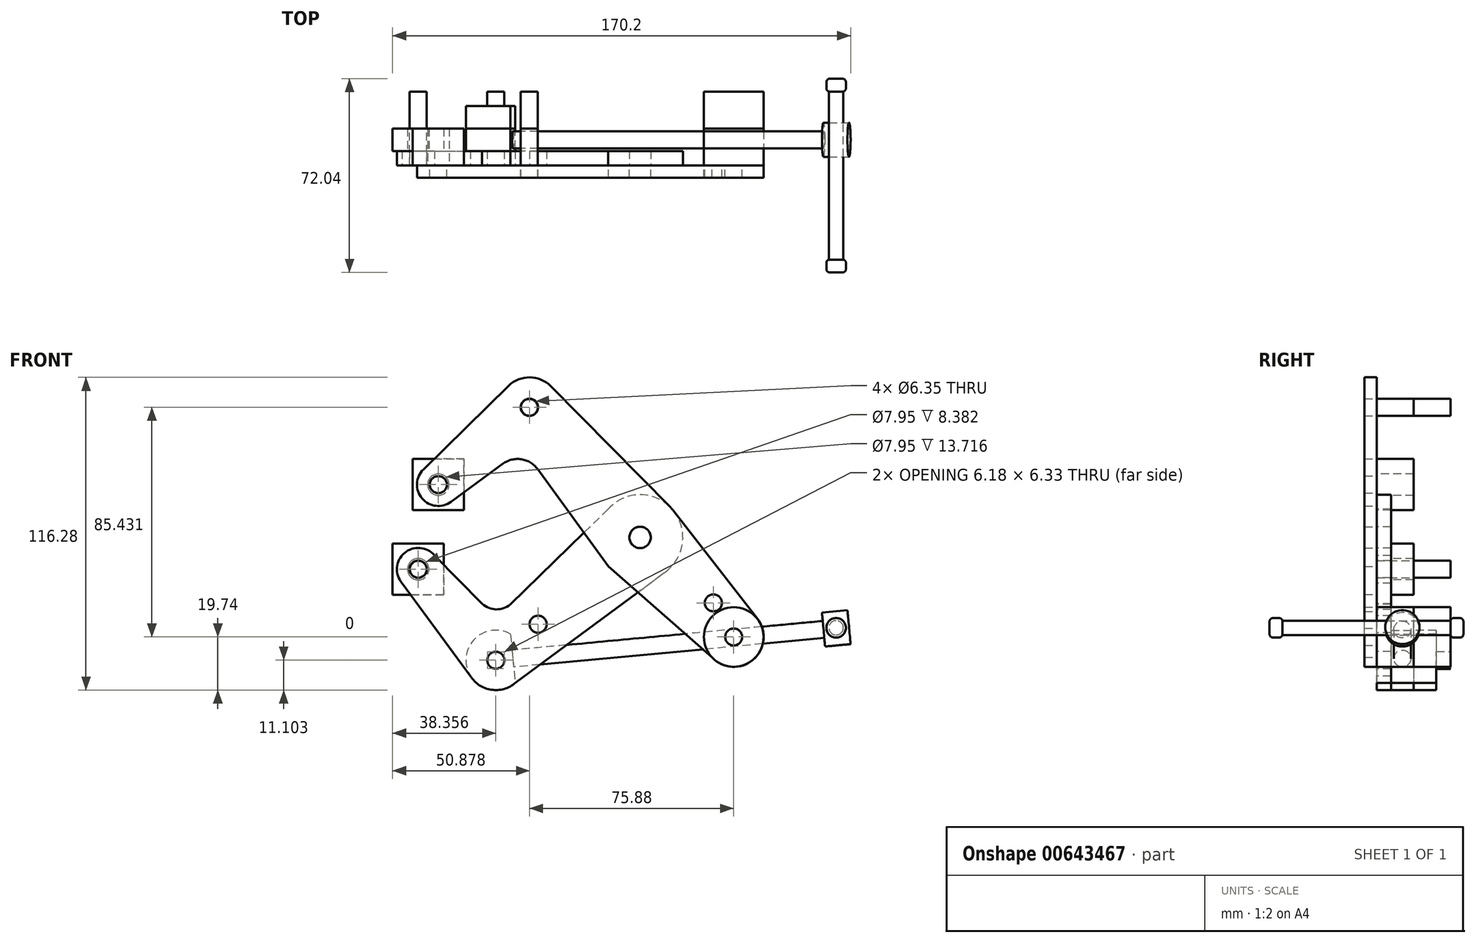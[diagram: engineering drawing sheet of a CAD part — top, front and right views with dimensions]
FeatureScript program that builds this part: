
annotation { "Feature Type Name" : "Feature", "Feature Type Description" : "" }
export const myFeature = defineFeature(function(context is Context, id is Id, definition is map)
    precondition{}
    {
        {
            var Q0;
            Q0=qCreatedBy(makeId("Front.planeOp"),FACE);
            var sketch = newSketch(context, id + "F0", { "sketchPlane" : qUnion([Q0])});
            skCircle(sketch, "E0", {"center": v(0, 0) * mm, "radius": 3.98 * mm});
            skCircle(sketch, "E1", {"center": v(0, 0) * mm, "radius": 15.88 * mm});
            skCircle(sketch, "E2", {"center": v(-41.1, 48.41) * mm, "radius": 11.11 * mm});
            skCircle(sketch, "E3", {"center": v(-41.1, 48.41) * mm, "radius": 3.18 * mm});
            skCircle(sketch, "E4", {"center": v(-74.97, 19.63) * mm, "radius": 3.18 * mm});
            skCircle(sketch, "E5", {"center": v(-74.97, 19.63) * mm, "radius": 7.94 * mm});
            skCircle(sketch, "E6", {"center": v(0, 0) * mm, "radius": 3.18 * mm});
            skCircle(sketch, "E7", {"center": v(34.79, -37.02) * mm, "radius": 3.18 * mm});
            skCircle(sketch, "E8", {"center": v(34.79, -37.02) * mm, "radius": 11.11 * mm});
            skLineSegment(sketch, "E9", {"start": v(-41.1, 48.41) * mm, "end": v(-74.97, 19.63) * mm, "construction": true});
            skLineSegment(sketch, "E10", {"start": v(-41.1, 48.41) * mm, "end": v(0, 0) * mm, "construction": true});
            skLineSegment(sketch, "E11", {"start": v(0, 0) * mm, "end": v(34.79, -37.02) * mm, "construction": true});
            skCircle(sketch, "E12", {"center": v(27.23, -24.34) * mm, "radius": 3.18 * mm});
            skLineSegment(sketch, "E13", {"start": v(-33.18, 56.22) * mm, "end": v(11.3, 11.15) * mm});
            skLineSegment(sketch, "E14", {"start": v(12.54, 9.74) * mm, "end": v(43.56, -30.2) * mm});
            skLineSegment(sketch, "E15", {"start": v(26.69, -44.63) * mm, "end": v(-11.8, -10.76) * mm});
            skLineSegment(sketch, "E16", {"start": v(-11.8, -10.76) * mm, "end": v(-38.09, 25.38) * mm});
            skLineSegment(sketch, "E17", {"start": v(-80.52, 25.3) * mm, "end": v(-48.87, 56.34) * mm});
            skPoint(sketch, "E18", {"position": v(-43.61, 32.78) * mm});
            skPoint(sketch, "E19", {"position": v(-80.25, 58.74) * mm});
            skArc(sketch, "E20", {"start": v(-38.09, 25.38) * mm, "mid": v(-44.1, 29.06) * mm, "end": v(-50.97, 27.39) * mm});
            skLineSegment(sketch, "E21", {"start": v(-50.97, 27.39) * mm, "end": v(-70.27, 13.23) * mm});
            skSolve(sketch);
        }
        {
            var Q0;
            Q0 = qSketchRegion(id + "F0", true);
            var Q1;
            {var subQ1=sQuery(id+"F0.wireOp",EDGE,"pfiCSikp-8CTO-SDfE-DP6H-Jw97YbxvFowv");var subQ3=sQuery(id+"F0.wireOp",EDGE,"inh5m93a-XSK5-ioNv-JxQd-0MRj083akBz5");var subQ4=makeQuery(id+"F0.imprint","INTERSECT",VERTEX,{"derivedFrom":[subQ1,subQ3]});Q1=makeQuery(id+"F0.imprint","IMPRINT",FACE,{"disambiguationData":[TD([[makeQuery(id+"F0.imprint","IMPRINT",EDGE,{"disambiguationData":[TD([[subQ4,1.0]])],"derivedFrom":subQ3}),-1.0]])]});}
            var Q2;
            {var subQ5=sQuery(id+"F0.wireOp",EDGE,"1JsmmwyK-uvK5-ssic-tOmo-jzBYzs2uoYHw");var subQ7=sQuery(id+"F0.wireOp",EDGE,"MQRNNOWK-pdrb-iC6u-Mh0e-8VP2wnjC3u4w");var subQ8=makeQuery(id+"F0.imprint","INTERSECT",VERTEX,{"derivedFrom":[subQ5,subQ7]});Q2=makeQuery(id+"F0.imprint","IMPRINT",FACE,{"disambiguationData":[TD([[makeQuery(id+"F0.imprint","IMPRINT",EDGE,{"disambiguationData":[TD([[subQ8,1.0]])],"derivedFrom":subQ5}),-1.0]])]});}
            extrude(context, id + "F1", {"entities" : qUnion([Q0, Q1, Q2]), "depth" : 4.57 * mm, "offsetDistance" : 25.4 * mm});
        }
        {
            var Q0;
            Q0=qCreatedBy(makeId("Front.planeOp"),FACE);
            var sketch = newSketch(context, id + "F2", { "sketchPlane" : qUnion([Q0])});
            skCircle(sketch, "E22", {"center": v(0, -0.01) * mm, "radius": 15.88 * mm});
            skCircle(sketch, "E23", {"center": v(-53.62, -45.66) * mm, "radius": 3.18 * mm});
            skCircle(sketch, "E24", {"center": v(-37.9, -32.27) * mm, "radius": 3.18 * mm});
            skCircle(sketch, "E25", {"center": v(-82.44, -11.83) * mm, "radius": 3.18 * mm});
            skCircle(sketch, "E26", {"center": v(-82.44, -11.83) * mm, "radius": 7.94 * mm});
            skLineSegment(sketch, "E27", {"start": v(-76.4, -6.68) * mm, "end": v(-76.4, -6.68) * mm});
            skLineSegment(sketch, "E28", {"start": v(-88.49, -16.97) * mm, "end": v(-62.08, -52.87) * mm});
            skLineSegment(sketch, "E29", {"start": v(-46.41, -54.12) * mm, "end": v(10.96, -11.66) * mm});
            skArc(sketch, "E30", {"start": v(-58.68, -24.7) * mm, "mid": v(-53.52, -26.75) * mm, "end": v(-48.26, -24.95) * mm});
            skPoint(sketch, "E31", {"position": v(-53.46, -30.01) * mm});
            skPoint(sketch, "E32", {"position": v(-10.2, 12.15) * mm});
            skLineSegment(sketch, "E33", {"start": v(-10.2, 12.15) * mm, "end": v(-48.26, -24.95) * mm});
            skPoint(sketch, "E34", {"position": v(-76.4, -6.68) * mm});
            skLineSegment(sketch, "E35", {"start": v(-76.4, -6.68) * mm, "end": v(-58.68, -24.7) * mm});
            skArc(sketch, "E36", {"start": v(-51.2, -43.6) * mm, "mid": v(-53.37, -42.5) * mm, "end": v(-55.68, -43.24) * mm});
            skArc(sketch, "E37", {"start": v(-62.08, -52.87) * mm, "mid": v(-54.5, -56.73) * mm, "end": v(-46.41, -54.12) * mm});
            skCircle(sketch, "E38", {"center": v(0, -0.01) * mm, "radius": 3.97 * mm});
            skCircle(sketch, "E39", {"center": v(-53.62, -45.63) * mm, "radius": 11.13 * mm});
            skLineSegment(sketch, "E40", {"start": v(0, 0) * mm, "end": v(-53.62, -45.63) * mm, "construction": true});
            skLineSegment(sketch, "E41", {"start": v(-53.62, -45.63) * mm, "end": v(-82.44, -11.83) * mm, "construction": true});
            skSolve(sketch);
        }
        {
            var Q0;
            Q0 = qSketchRegion(id + "F2", true);
            extrude(context, id + "F3", {"entities" : qUnion([Q0]), "oppositeDirection" : true, "depth" : 5.33 * mm, "offsetDistance" : 25.4 * mm});
        }
        {
            var Q0;
            Q0=qCreatedBy(makeId("Front.planeOp"),FACE);
            cPlane(context, id + "F4", {"entities" : qUnion([Q0]), "cplaneType" : CPlaneType.OFFSET, "offset" : 13.72 * mm, "oppositeDirection" : true, "width" : 152.4 * mm, "height" : 152.4 * mm});
        }
        {
            var Q0;
            Q0=qCreatedBy(id+"F4.planeOp",FACE);
            var sketch = newSketch(context, id + "F5", { "sketchPlane" : qUnion([Q0])});
            skArc(sketch, "E42", {"start": v(-48.14, -35.95) * mm, "mid": v(-64.68, -46.66) * mm, "end": v(-46.44, -54.11) * mm});
            skLineSegment(sketch, "E43", {"start": v(-48.14, -35.95) * mm, "end": v(-46.44, -54.11) * mm});
            skCircle(sketch, "E44", {"center": v(-82.44, -11.83) * mm, "radius": 3.18 * mm});
            skSolve(sketch);
        }
        {
            var Q0;
            Q0 = qSketchRegion(id + "F5", true);
            var Q1;
            Q1=makeQuery(id+"F3.opExtrude","CAP_FACE",FACE,{"disambiguationData":[OSD([sQuery(id+"F2.wireOp",EDGE,"E22"),sQuery(id+"F2.wireOp",EDGE,"E23"),sQuery(id+"F2.wireOp",EDGE,"E24"),sQuery(id+"F2.wireOp",EDGE,"E25"),sQuery(id+"F2.wireOp",EDGE,"E26"),sQuery(id+"F2.wireOp",EDGE,"E28"),sQuery(id+"F2.wireOp",EDGE,"E29"),sQuery(id+"F2.wireOp",EDGE,"E30"),sQuery(id+"F2.wireOp",EDGE,"E33"),sQuery(id+"F2.wireOp",EDGE,"E35"),sQuery(id+"F2.wireOp",EDGE,"E36"),sQuery(id+"F2.wireOp",EDGE,"E37"),sQuery(id+"F2.wireOp",EDGE,"E38")])],"isStart":true});
            extrude(context, id + "F6", {"entities" : qUnion([Q0]), "endBound" : BoundingType.UP_TO_SURFACE, "depth" : 5.6 * mm, "endBoundEntityFace" : qUnion([Q1]), "offsetDistance" : 25.4 * mm});
        }
        {
            var Q0;
            Q0=qCreatedBy(makeId("Front.planeOp"),FACE);
            var sketch = newSketch(context, id + "F7", { "sketchPlane" : qUnion([Q0])});
            skCircle(sketch, "E45", {"center": v(34.79, -37.02) * mm, "radius": 11.06 * mm});
            skCircle(sketch, "E46", {"center": v(-41.18, 48.34) * mm, "radius": 3.17 * mm});
            skSolve(sketch);
        }
        {
            var Q0;
            Q0 = qSketchRegion(id + "F7", true);
            var Q1;
            Q1=qCreatedBy(id+"F4.planeOp",FACE);
            extrude(context, id + "F8", {"entities" : qUnion([Q0]), "endBound" : BoundingType.UP_TO_SURFACE, "oppositeDirection" : true, "depth" : 10.92 * mm, "endBoundEntityFace" : qUnion([Q1]), "offsetDistance" : 25.4 * mm});
        }
        {
            var Q0;
            Q0 = qSketchRegion(id + "F7", true);
            var Q1;
            Q1=makeQuery(id+"F1.opExtrude","CAP_FACE",FACE,{"disambiguationData":[OSD([sQuery(id+"F0.wireOp",EDGE,"E0"),sQuery(id+"F0.wireOp",EDGE,"E1"),sQuery(id+"F0.wireOp",EDGE,"E2"),sQuery(id+"F0.wireOp",EDGE,"E3"),sQuery(id+"F0.wireOp",EDGE,"E4"),sQuery(id+"F0.wireOp",EDGE,"E5"),sQuery(id+"F0.wireOp",EDGE,"E7"),sQuery(id+"F0.wireOp",EDGE,"E8"),sQuery(id+"F0.wireOp",EDGE,"E12"),sQuery(id+"F0.wireOp",EDGE,"E13"),sQuery(id+"F0.wireOp",EDGE,"E14"),sQuery(id+"F0.wireOp",EDGE,"E15"),sQuery(id+"F0.wireOp",EDGE,"E16"),sQuery(id+"F0.wireOp",EDGE,"DcXNMXHQ-oR97-Upbm-TpGR-8wW1jvlWBgT4"),sQuery(id+"F0.wireOp",EDGE,"E17"),sQuery(id+"F0.wireOp",EDGE,"E20")])],"isStart":false});
            extrude(context, id + "F9", {"entities" : qUnion([Q0]), "endBound" : BoundingType.UP_TO_SURFACE, "depth" : 19.3 * mm, "endBoundEntityFace" : qUnion([Q1]), "offsetDistance" : 25.4 * mm});
        }
        {
            var Q0;
            Q0=sQuery(id+"F5.wireOp",EDGE,"E43");
            var Q1;
            Q1=sQuery(id+"F5.wireOp",EDGE,"E42");
            var Q2;
            Q2=makeQuery(id+"F3.opExtrude","CAP_FACE",FACE,{"disambiguationData":[OSD([sQuery(id+"F2.wireOp",EDGE,"E22"),sQuery(id+"F2.wireOp",EDGE,"E23"),sQuery(id+"F2.wireOp",EDGE,"E24"),sQuery(id+"F2.wireOp",EDGE,"E25"),sQuery(id+"F2.wireOp",EDGE,"E26"),sQuery(id+"F2.wireOp",EDGE,"E28"),sQuery(id+"F2.wireOp",EDGE,"E29"),sQuery(id+"F2.wireOp",EDGE,"E30"),sQuery(id+"F2.wireOp",EDGE,"E33"),sQuery(id+"F2.wireOp",EDGE,"E35"),sQuery(id+"F2.wireOp",EDGE,"E36"),sQuery(id+"F2.wireOp",EDGE,"E37"),sQuery(id+"F2.wireOp",EDGE,"E38")])],"isStart":true});
            extrude(context, id + "F10", {"bodyType" : ToolBodyType.SURFACE, "surfaceEntities" : qUnion([Q0, Q1]), "endBound" : BoundingType.UP_TO_SURFACE, "depth" : 18.67 * mm, "endBoundEntityFace" : qUnion([Q2]), "offsetDistance" : 25.4 * mm});
        }
        {
            var Q0;
            Q0=makeQuery(id+"F10.opExtrude","SWEPT_FACE",FACE,{"disambiguationData":[OSD([sQuery(id+"F5.wireOp",EDGE,"E43")])]});
            var sketch = newSketch(context, id + "F11", { "sketchPlane" : qUnion([Q0])});
            skCircle(sketch, "E47", {"center": v(-9.52, -40.43) * mm, "radius": 3.18 * mm});
            skLineSegment(sketch, "E48", {"start": v(-13.72, -40.43) * mm, "end": v(-5.33, -40.43) * mm});
            skSolve(sketch);
        }
        {
            var Q0;
            Q0 = qSketchRegion(id + "F11", true);
            extrude(context, id + "F12", {"entities" : qUnion([Q0]), "oppositeDirection" : true, "depth" : 125.48 * mm, "offsetDistance" : 25.4 * mm});
        }
        {
            var Q0;
            Q0=makeQuery(id+"F12.opExtrude","CAP_FACE",FACE,{"disambiguationData":[OSD([sQuery(id+"F11.wireOp",EDGE,"E47")])],"isStart":false});
            var sketch = newSketch(context, id + "F13", { "sketchPlane" : qUnion([Q0])});
            skCircle(sketch, "E49", {"center": v(9.52, -40.43) * mm, "radius": 6.35 * mm});
            skSolve(sketch);
        }
        {
            var Q0;
            Q0=makeQuery(id+"F13.imprint","IMPRINT",FACE,{"disambiguationData":[TD([[makeQuery(id+"F13.imprint","IMPRINT",EDGE,{"derivedFrom":sQuery(id+"F13.wireOp",EDGE,"E49")}),1.0]])]});
            extrude(context, id + "F14", {"entities" : qUnion([Q0]), "operationType" : NewBodyOperationType.ADD, "oppositeDirection" : true, "depth" : 9.52 * mm, "offsetDistance" : 25.4 * mm});
        }
        {
            var Q0;
            Q0=makeQuery(id+"F1.opExtrude","SWEPT_BODY",BODY,{"disambiguationData":[OSD([sQuery(id+"F0.wireOp",EDGE,"E0"),sQuery(id+"F0.wireOp",EDGE,"E1"),sQuery(id+"F0.wireOp",EDGE,"E2"),sQuery(id+"F0.wireOp",EDGE,"E3"),sQuery(id+"F0.wireOp",EDGE,"E4"),sQuery(id+"F0.wireOp",EDGE,"E5"),sQuery(id+"F0.wireOp",EDGE,"E7"),sQuery(id+"F0.wireOp",EDGE,"E8"),sQuery(id+"F0.wireOp",EDGE,"E12"),sQuery(id+"F0.wireOp",EDGE,"E13"),sQuery(id+"F0.wireOp",EDGE,"E14"),sQuery(id+"F0.wireOp",EDGE,"E15"),sQuery(id+"F0.wireOp",EDGE,"E16"),sQuery(id+"F0.wireOp",EDGE,"E17"),sQuery(id+"F0.wireOp",EDGE,"E20"),sQuery(id+"F0.wireOp",EDGE,"E21")])]});
            var Q1;
            Q1=makeQuery(id+"F3.opExtrude","SWEPT_BODY",BODY,{"disambiguationData":[OSD([sQuery(id+"F2.wireOp",EDGE,"E22"),sQuery(id+"F2.wireOp",EDGE,"E23"),sQuery(id+"F2.wireOp",EDGE,"E24"),sQuery(id+"F2.wireOp",EDGE,"E25"),sQuery(id+"F2.wireOp",EDGE,"E26"),sQuery(id+"F2.wireOp",EDGE,"E28"),sQuery(id+"F2.wireOp",EDGE,"E29"),sQuery(id+"F2.wireOp",EDGE,"E30"),sQuery(id+"F2.wireOp",EDGE,"E33"),sQuery(id+"F2.wireOp",EDGE,"E35"),sQuery(id+"F2.wireOp",EDGE,"E36"),sQuery(id+"F2.wireOp",EDGE,"E38"),sQuery(id+"F2.wireOp",EDGE,"E39")])]});
            var Q2;
            Q2=makeQuery(id+"F8.opExtrude","SWEPT_BODY",BODY,{"disambiguationData":[OSD([sQuery(id+"F7.wireOp",EDGE,"E45")])]});
            var Q3;
            Q3=makeQuery(id+"F6.opExtrude","SWEPT_BODY",BODY,{"disambiguationData":[OSD([sQuery(id+"F5.wireOp",EDGE,"E42"),sQuery(id+"F5.wireOp",EDGE,"E43")])]});
            var Q4;
            Q4=makeQuery(id+"F6.opExtrude","SWEPT_BODY",BODY,{"disambiguationData":[OSD([sQuery(id+"F5.wireOp",EDGE,"E44")])]});
            var Q5;
            Q5=makeQuery(id+"F8.opExtrude","SWEPT_BODY",BODY,{"disambiguationData":[OSD([sQuery(id+"F7.wireOp",EDGE,"E46")])]});
            booleanBodies(context, id + "F15", {"operationType" : BooleanOperationType.SUBTRACTION, "tools" : qUnion([Q0, Q1]), "targets" : qUnion([Q2, Q3, Q4, Q5]), "keepTools" : true});
        }
        {
            var Q0;
            Q0=makeQuery(id+"F8.opExtrude","SWEPT_BODY",BODY,{"disambiguationData":[OSD([sQuery(id+"F7.wireOp",EDGE,"E46")])]});
            var Q1;
            Q1=makeQuery(id+"F6.opExtrude","SWEPT_BODY",BODY,{"disambiguationData":[OSD([sQuery(id+"F5.wireOp",EDGE,"E44")])]});
            var Q2;
            Q2=makeQuery(id+"F6.opExtrude","SWEPT_BODY",BODY,{"disambiguationData":[OSD([sQuery(id+"F5.wireOp",EDGE,"E42"),sQuery(id+"F5.wireOp",EDGE,"E43")])]});
            var Q3;
            Q3=makeQuery(id+"F8.opExtrude","SWEPT_BODY",BODY,{"disambiguationData":[OSD([sQuery(id+"F7.wireOp",EDGE,"E45")])]});
            var Q4;
            Q4=qCreatedBy(id+"F4.planeOp",FACE);
            mirror(context, id + "F16", {"entities" : qUnion([Q0, Q1, Q2, Q3]), "mirrorPlane" : qUnion([Q4])});
        }
        {
            var Q0;
            Q0=makeQuery(id+"F16.opPattern","COPY",FACE,{"derivedFrom":makeQuery(id+"F8.opExtrude","CAP_FACE",FACE,{"disambiguationData":[OSD([sQuery(id+"F7.wireOp",EDGE,"E45")])],"isStart":true}),"instanceName":"1"});
            cPlane(context, id + "F17", {"entities" : qUnion([Q0]), "cplaneType" : CPlaneType.OFFSET, "offset" : 0 * mm, "width" : 152.4 * mm, "height" : 152.4 * mm});
        }
        {
            var Q0;
            Q0=qCreatedBy(id+"F17.planeOp",FACE);
            var sketch = newSketch(context, id + "F18", { "sketchPlane" : qUnion([Q0])});
            skCircle(sketch, "E50", {"center": v(-72.85, -33.6) * mm, "radius": 2.67 * mm});
            skSolve(sketch);
        }
        {
            var Q0;
            Q0 = qSketchRegion(id + "F18", true);
            extrude(context, id + "F19", {"entities" : qUnion([Q0]), "oppositeDirection" : true, "depth" : 62.48 * mm, "offsetDistance" : 25.4 * mm});
        }
        {
            var Q0;
            Q0=makeQuery(id+"F19.opExtrude","CAP_FACE",FACE,{"disambiguationData":[OSD([sQuery(id+"F18.wireOp",EDGE,"E50")])],"isStart":true});
            var sketch = newSketch(context, id + "F20", { "sketchPlane" : qUnion([Q0])});
            skCircle(sketch, "E51", {"center": v(-72.85, -33.6) * mm, "radius": 3.63 * mm});
            skSolve(sketch);
        }
        {
            var Q0;
            Q0 = qSketchRegion(id + "F20", true);
            extrude(context, id + "F21", {"entities" : qUnion([Q0]), "operationType" : NewBodyOperationType.ADD, "depth" : 4.78 * mm, "offsetDistance" : 25.4 * mm});
        }
        {
            var Q0;
            Q0=makeQuery(id+"F19.opExtrude","CAP_FACE",FACE,{"disambiguationData":[OSD([sQuery(id+"F18.wireOp",EDGE,"E50")])],"isStart":false});
            var sketch = newSketch(context, id + "F22", { "sketchPlane" : qUnion([Q0])});
            skCircle(sketch, "E52", {"center": v(72.85, -33.6) * mm, "radius": 3.63 * mm});
            skSolve(sketch);
        }
        {
            var Q0;
            Q0 = qSketchRegion(id + "F22", true);
            extrude(context, id + "F23", {"entities" : qUnion([Q0]), "operationType" : NewBodyOperationType.ADD, "depth" : 4.78 * mm, "offsetDistance" : 25.4 * mm});
        }
        {
            var Q0;
            Q0=makeQuery(id+"F23.opExtrude","CAP_EDGE",EDGE,{"disambiguationData":[OSD([sQuery(id+"F22.wireOp",EDGE,"E52")])],"isStart":false});
            fillet(context, id + "F24", {"entities" : qUnion([Q0]), "radius" : 1.27 * mm, "tangentPropagation" : true, "allowEdgeOverflow" : false});
        }
        {
            var Q0;
            Q0=makeQuery(id+"F21.opExtrude","CAP_EDGE",EDGE,{"disambiguationData":[OSD([sQuery(id+"F20.wireOp",EDGE,"E51")])],"isStart":false});
            fillet(context, id + "F25", {"entities" : qUnion([Q0]), "radius" : 1.27 * mm, "tangentPropagation" : true, "allowEdgeOverflow" : false});
        }
        {
            var Q0;
            Q0=makeQuery(id+"F23.opExtrude","CAP_EDGE",EDGE,{"disambiguationData":[OSD([sQuery(id+"F22.wireOp",EDGE,"E52")])],"isStart":true});
            fillet(context, id + "F26", {"entities" : qUnion([Q0]), "radius" : 1.27 * mm, "tangentPropagation" : true, "allowEdgeOverflow" : false});
        }
        {
            var Q0;
            Q0=makeQuery(id+"F21.opExtrude","CAP_EDGE",EDGE,{"disambiguationData":[OSD([sQuery(id+"F20.wireOp",EDGE,"E51")])],"isStart":true});
            fillet(context, id + "F27", {"entities" : qUnion([Q0]), "radius" : 1.27 * mm, "tangentPropagation" : true, "allowEdgeOverflow" : false});
        }
        {
            var Q0;
            Q0=makeQuery(id+"F3.opExtrude","CAP_FACE",FACE,{"disambiguationData":[OSD([sQuery(id+"F2.wireOp",EDGE,"E22"),sQuery(id+"F2.wireOp",EDGE,"E23"),sQuery(id+"F2.wireOp",EDGE,"E24"),sQuery(id+"F2.wireOp",EDGE,"E25"),sQuery(id+"F2.wireOp",EDGE,"E26"),sQuery(id+"F2.wireOp",EDGE,"E28"),sQuery(id+"F2.wireOp",EDGE,"E29"),sQuery(id+"F2.wireOp",EDGE,"E30"),sQuery(id+"F2.wireOp",EDGE,"E33"),sQuery(id+"F2.wireOp",EDGE,"E35"),sQuery(id+"F2.wireOp",EDGE,"E36"),sQuery(id+"F2.wireOp",EDGE,"E38"),sQuery(id+"F2.wireOp",EDGE,"E39")])],"isStart":false});
            var sketch = newSketch(context, id + "F28", { "sketchPlane" : qUnion([Q0])});
            skLineSegment(sketch, "E53.bottom", {"start": v(91.97, -2.3) * mm, "end": v(72.92, -2.3) * mm});
            skLineSegment(sketch, "E53.top", {"start": v(91.97, -21.35) * mm, "end": v(72.92, -21.35) * mm});
            skLineSegment(sketch, "E53.left", {"start": v(91.97, -2.3) * mm, "end": v(91.97, -21.35) * mm});
            skLineSegment(sketch, "E53.right", {"start": v(72.92, -2.3) * mm, "end": v(72.92, -21.35) * mm});
            skPoint(sketch, "E53.middle", {"position": v(82.44, -11.83) * mm});
            skCircle(sketch, "E54", {"center": v(82.44, -11.83) * mm, "radius": 3.98 * mm});
            skSolve(sketch);
        }
        {
            var Q0;
            Q0=makeQuery(id+"F1.opExtrude","CAP_FACE",FACE,{"disambiguationData":[OSD([sQuery(id+"F0.wireOp",EDGE,"E0"),sQuery(id+"F0.wireOp",EDGE,"E1"),sQuery(id+"F0.wireOp",EDGE,"E2"),sQuery(id+"F0.wireOp",EDGE,"E3"),sQuery(id+"F0.wireOp",EDGE,"E4"),sQuery(id+"F0.wireOp",EDGE,"E5"),sQuery(id+"F0.wireOp",EDGE,"E7"),sQuery(id+"F0.wireOp",EDGE,"E8"),sQuery(id+"F0.wireOp",EDGE,"E12"),sQuery(id+"F0.wireOp",EDGE,"E13"),sQuery(id+"F0.wireOp",EDGE,"E14"),sQuery(id+"F0.wireOp",EDGE,"E15"),sQuery(id+"F0.wireOp",EDGE,"E16"),sQuery(id+"F0.wireOp",EDGE,"E17"),sQuery(id+"F0.wireOp",EDGE,"E20"),sQuery(id+"F0.wireOp",EDGE,"E21")])],"isStart":true});
            var sketch = newSketch(context, id + "F29", { "sketchPlane" : qUnion([Q0])});
            skLineSegment(sketch, "E55.bottom", {"start": v(84.5, 29.16) * mm, "end": v(65.44, 29.16) * mm});
            skLineSegment(sketch, "E55.top", {"start": v(84.5, 10.1) * mm, "end": v(65.44, 10.1) * mm});
            skLineSegment(sketch, "E55.left", {"start": v(84.5, 29.16) * mm, "end": v(84.5, 10.1) * mm});
            skLineSegment(sketch, "E55.right", {"start": v(65.44, 29.16) * mm, "end": v(65.44, 10.1) * mm});
            skPoint(sketch, "E55.middle", {"position": v(74.97, 19.63) * mm});
            skCircle(sketch, "E56", {"center": v(74.97, 19.63) * mm, "radius": 3.98 * mm});
            skSolve(sketch);
        }
        {
            var Q0;
            {var subQ1=sQuery(id+"F29.wireOp",EDGE,"E55.top");Q0=makeQuery(id+"F29.imprint","IMPRINT",FACE,{"disambiguationData":[TD([[makeQuery(id+"F29.imprint","IMPRINT",EDGE,{"derivedFrom":subQ1}),-1.0]])]});}
            var Q1;
            Q1=makeQuery(id+"F29.imprint","IMPRINT",FACE,{"disambiguationData":[TD([[makeQuery(id+"F29.imprint","IMPRINT",EDGE,{"derivedFrom":sQuery(id+"F29.wireOp",EDGE,"E56")}),-1.0]])]});
            var Q2;
            {var subQ1=sQuery(id+"F28.wireOp",EDGE,"E53.bottom");Q2=makeQuery(id+"F28.imprint","IMPRINT",FACE,{"disambiguationData":[TD([[makeQuery(id+"F28.imprint","IMPRINT",EDGE,{"derivedFrom":subQ1}),1.0]])]});}
            var Q3;
            Q3=makeQuery(id+"F28.imprint","IMPRINT",FACE,{"disambiguationData":[TD([[makeQuery(id+"F28.imprint","IMPRINT",EDGE,{"derivedFrom":sQuery(id+"F28.wireOp",EDGE,"E54")}),-1.0]])]});
            var Q4;
            Q4=qCreatedBy(id+"F4.planeOp",FACE);
            extrude(context, id + "F30", {"entities" : qUnion([Q0, Q1, Q2, Q3]), "operationType" : NewBodyOperationType.ADD, "endBound" : BoundingType.UP_TO_SURFACE, "depth" : 25.4 * mm, "endBoundEntityFace" : qUnion([Q4]), "offsetDistance" : 25.4 * mm});
        }
    });
